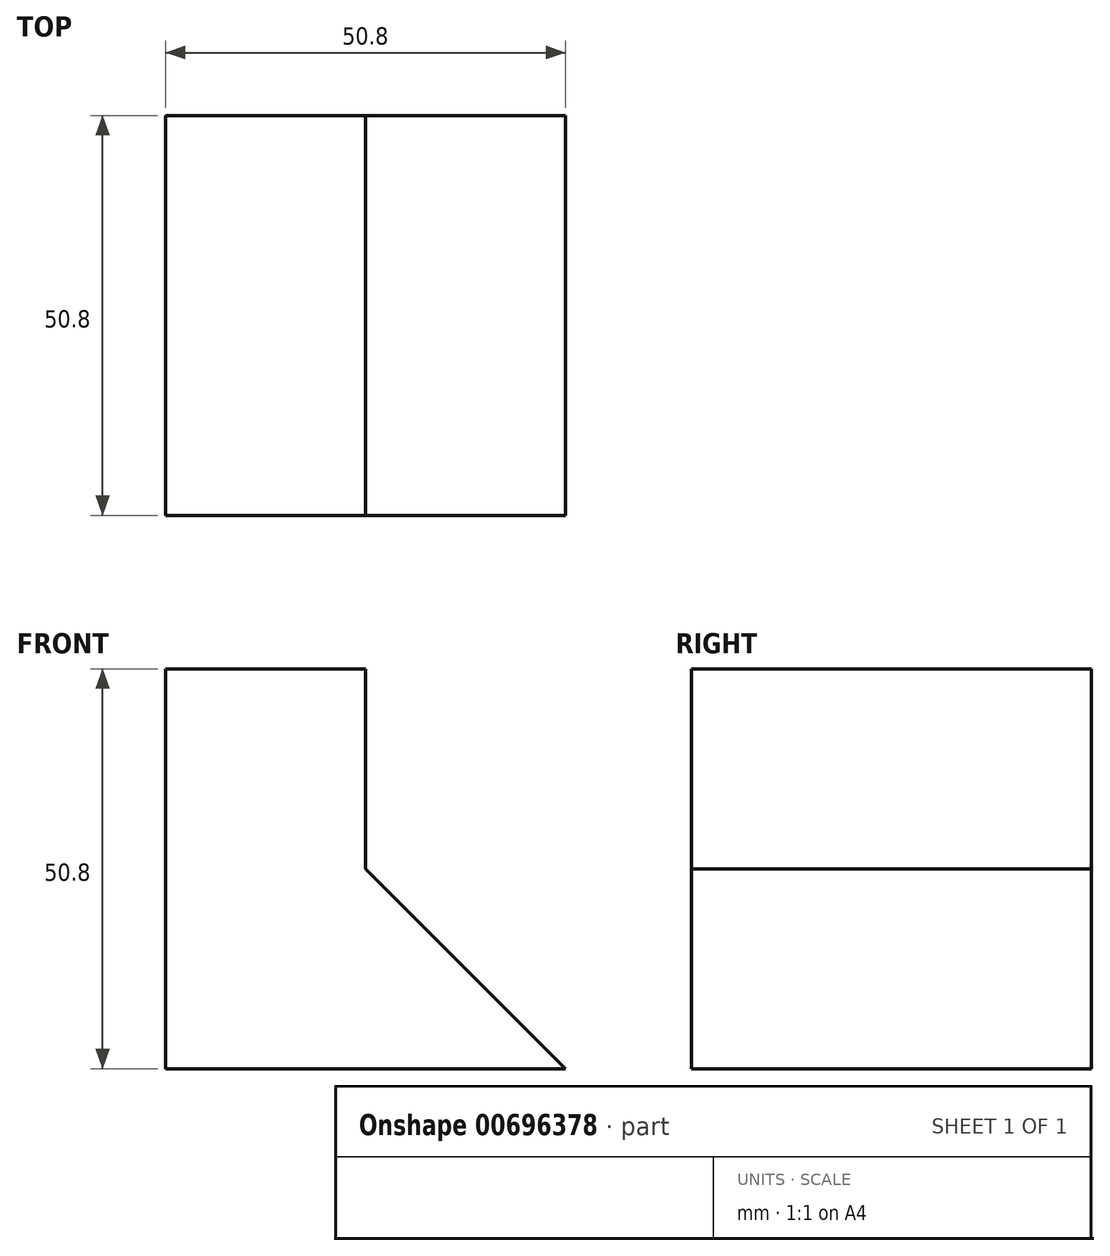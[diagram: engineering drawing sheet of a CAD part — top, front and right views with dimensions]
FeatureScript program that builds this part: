
annotation { "Feature Type Name" : "Feature", "Feature Type Description" : "" }
export const myFeature = defineFeature(function(context is Context, id is Id, definition is map)
    precondition{}
    {
        {
            var Q0;
            Q0=qCreatedBy(makeId("Front.planeOp"),FACE);
            var sketch = newSketch(context, id + "F0", { "sketchPlane" : qUnion([Q0])});
            skLineSegment(sketch, "E0.bottom", {"start": v(0, 0) * mm, "end": v(-50.8, 0) * mm});
            skLineSegment(sketch, "E0.top", {"start": v(-25.4, 50.8) * mm, "end": v(-50.8, 50.8) * mm});
            skLineSegment(sketch, "E0.right", {"start": v(-50.8, 0) * mm, "end": v(-50.8, 50.8) * mm});
            skLineSegment(sketch, "E1", {"start": v(-25.4, 50.8) * mm, "end": v(-25.4, 25.4) * mm});
            skLineSegment(sketch, "E2", {"start": v(0, 0) * mm, "end": v(-25.4, 25.4) * mm});
            skPoint(sketch, "E0.left.end.orphan", {"position": v(0, 50.8) * mm});
            skSolve(sketch);
        }
        {
            var Q0;
            Q0=makeQuery(id+"F0.imprint","IMPRINT",FACE,{"disambiguationData":[TD([[makeQuery(id+"F0.imprint","IMPRINT",EDGE,{"derivedFrom":sQuery(id+"F0.wireOp",EDGE,"E0.bottom")}),-1.0]])]});
            extrude(context, id + "F1", {"entities" : qUnion([Q0]), "depth" : 50.8 * mm, "offsetDistance" : 25.4 * mm});
        }
    });
